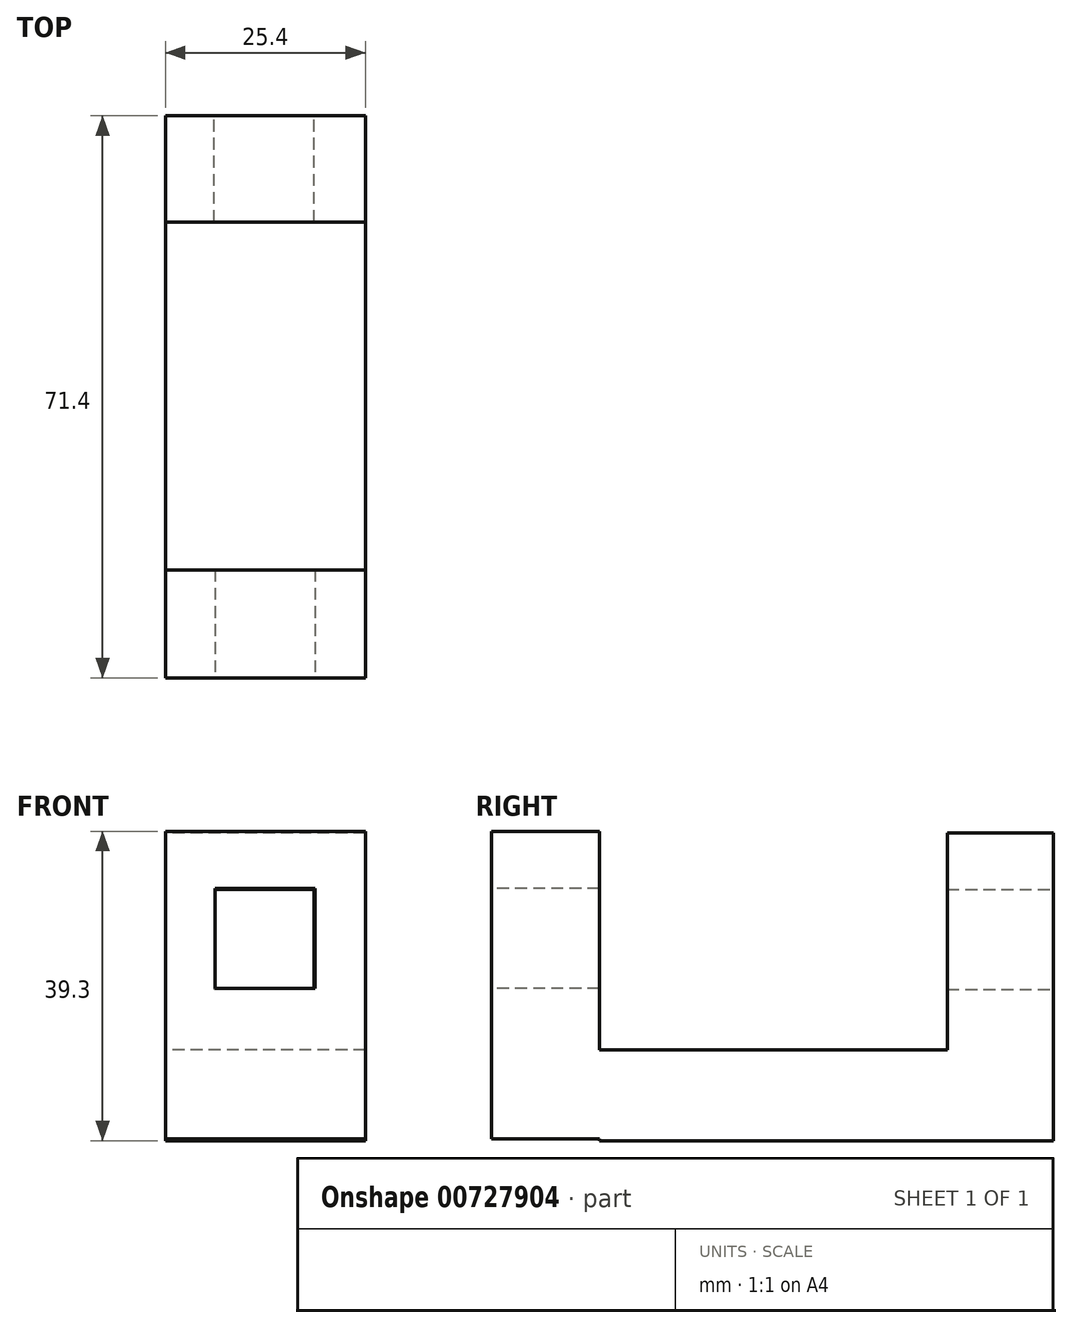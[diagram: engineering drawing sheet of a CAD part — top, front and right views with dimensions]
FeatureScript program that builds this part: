
annotation { "Feature Type Name" : "Feature", "Feature Type Description" : "" }
export const myFeature = defineFeature(function(context is Context, id is Id, definition is map)
    precondition{}
    {
        {
            var Q0;
            Q0=qCreatedBy(makeId("Right.planeOp"),FACE);
            var sketch = newSketch(context, id + "F0", { "sketchPlane" : qUnion([Q0])});
            skLineSegment(sketch, "E0.bottom", {"start": v(-34.77, 27.8) * mm, "end": v(-21.05, 27.8) * mm});
            skLineSegment(sketch, "E0.top", {"start": v(-34.77, -11.28) * mm, "end": v(-21.05, -11.28) * mm});
            skLineSegment(sketch, "E0.left", {"start": v(-34.77, 27.8) * mm, "end": v(-34.77, -11.28) * mm});
            skLineSegment(sketch, "E1.bottom", {"start": v(-21.05, 0) * mm, "end": v(23.14, 0) * mm});
            skLineSegment(sketch, "E1.top", {"start": v(-21.05, -11.51) * mm, "end": v(23.14, -11.51) * mm});
            skLineSegment(sketch, "E1.left", {"start": v(-21.05, -11.28) * mm, "end": v(-21.05, -11.51) * mm});
            skLineSegment(sketch, "E2.bottom", {"start": v(23.14, -11.51) * mm, "end": v(36.63, -11.51) * mm});
            skLineSegment(sketch, "E2.top", {"start": v(23.14, 27.56) * mm, "end": v(36.63, 27.56) * mm});
            skLineSegment(sketch, "E2.left", {"start": v(23.14, 0) * mm, "end": v(23.14, 27.56) * mm});
            skLineSegment(sketch, "E2.right", {"start": v(36.63, -11.51) * mm, "end": v(36.63, 27.56) * mm});
            skLineSegment(sketch, "E3", {"start": v(-21.05, 27.8) * mm, "end": v(-21.05, 0) * mm});
            skSolve(sketch);
        }
        {
            var Q0;
            Q0=makeQuery(id+"F0.imprint","IMPRINT",FACE,{"disambiguationData":[TD([[makeQuery(id+"F0.imprint","IMPRINT",EDGE,{"derivedFrom":sQuery(id+"F0.wireOp",EDGE,"E0.bottom")}),-1.0]])]});
            extrude(context, id + "F1", {"entities" : qUnion([Q0]), "depth" : 25.4 * mm, "offsetDistance" : 25.4 * mm});
        }
        {
            var Q0;
            Q0=makeQuery(id+"F0.imprint","IMPRINT",FACE,{"disambiguationData":[TD([[makeQuery(id+"F0.imprint","IMPRINT",EDGE,{"derivedFrom":sQuery(id+"F0.wireOp",EDGE,"E0.bottom")}),-1.0]])]});
            extrude(context, id + "F2", {"entities" : qUnion([Q0]), "operationType" : NewBodyOperationType.ADD, "depth" : 25.4 * mm, "offsetDistance" : 25.4 * mm});
        }
        {
            var Q0;
            Q0=makeQuery(id+"F1.opExtrude","SWEPT_FACE",FACE,{"disambiguationData":[OSD([sQuery(id+"F0.wireOp",EDGE,"E0.left")])]});
            var sketch = newSketch(context, id + "F3", { "sketchPlane" : qUnion([Q0])});
            skLineSegment(sketch, "E4.bottom", {"start": v(6.3, 20.55) * mm, "end": v(19, 20.55) * mm});
            skLineSegment(sketch, "E4.top", {"start": v(6.3, 7.85) * mm, "end": v(19, 7.85) * mm});
            skLineSegment(sketch, "E4.left", {"start": v(6.3, 20.55) * mm, "end": v(6.3, 7.85) * mm});
            skLineSegment(sketch, "E4.right", {"start": v(19, 20.55) * mm, "end": v(19, 7.85) * mm});
            skSolve(sketch);
        }
        {
            var Q0;
            Q0=makeQuery(id+"F3.imprint","IMPRINT",FACE,{"disambiguationData":[TD([[makeQuery(id+"F3.imprint","IMPRINT",EDGE,{"derivedFrom":sQuery(id+"F3.wireOp",EDGE,"E4.bottom")}),-1.0]])]});
            extrude(context, id + "F4", {"entities" : qUnion([Q0]), "operationType" : NewBodyOperationType.REMOVE, "oppositeDirection" : true, "depth" : 50.8 * mm, "offsetDistance" : 25.4 * mm});
        }
        {
            var Q0;
            Q0=makeQuery(id+"F1.opExtrude","SWEPT_FACE",FACE,{"disambiguationData":[OSD([sQuery(id+"F0.wireOp",EDGE,"E2.right")])]});
            var sketch = newSketch(context, id + "F5", { "sketchPlane" : qUnion([Q0])});
            skLineSegment(sketch, "E5.bottom", {"start": v(-18.86, 20.41) * mm, "end": v(-6.16, 20.41) * mm});
            skLineSegment(sketch, "E5.top", {"start": v(-18.86, 7.71) * mm, "end": v(-6.16, 7.71) * mm});
            skLineSegment(sketch, "E5.left", {"start": v(-18.86, 20.41) * mm, "end": v(-18.86, 7.71) * mm});
            skLineSegment(sketch, "E5.right", {"start": v(-6.16, 20.41) * mm, "end": v(-6.16, 7.71) * mm});
            skSolve(sketch);
        }
        {
            var Q0;
            Q0=qSketchRegion(id+"F5",true);
            extrude(context, id + "F6", {"entities" : qUnion([Q0]), "operationType" : NewBodyOperationType.REMOVE, "oppositeDirection" : true, "depth" : 50.8 * mm, "offsetDistance" : 25.4 * mm});
        }
    });
